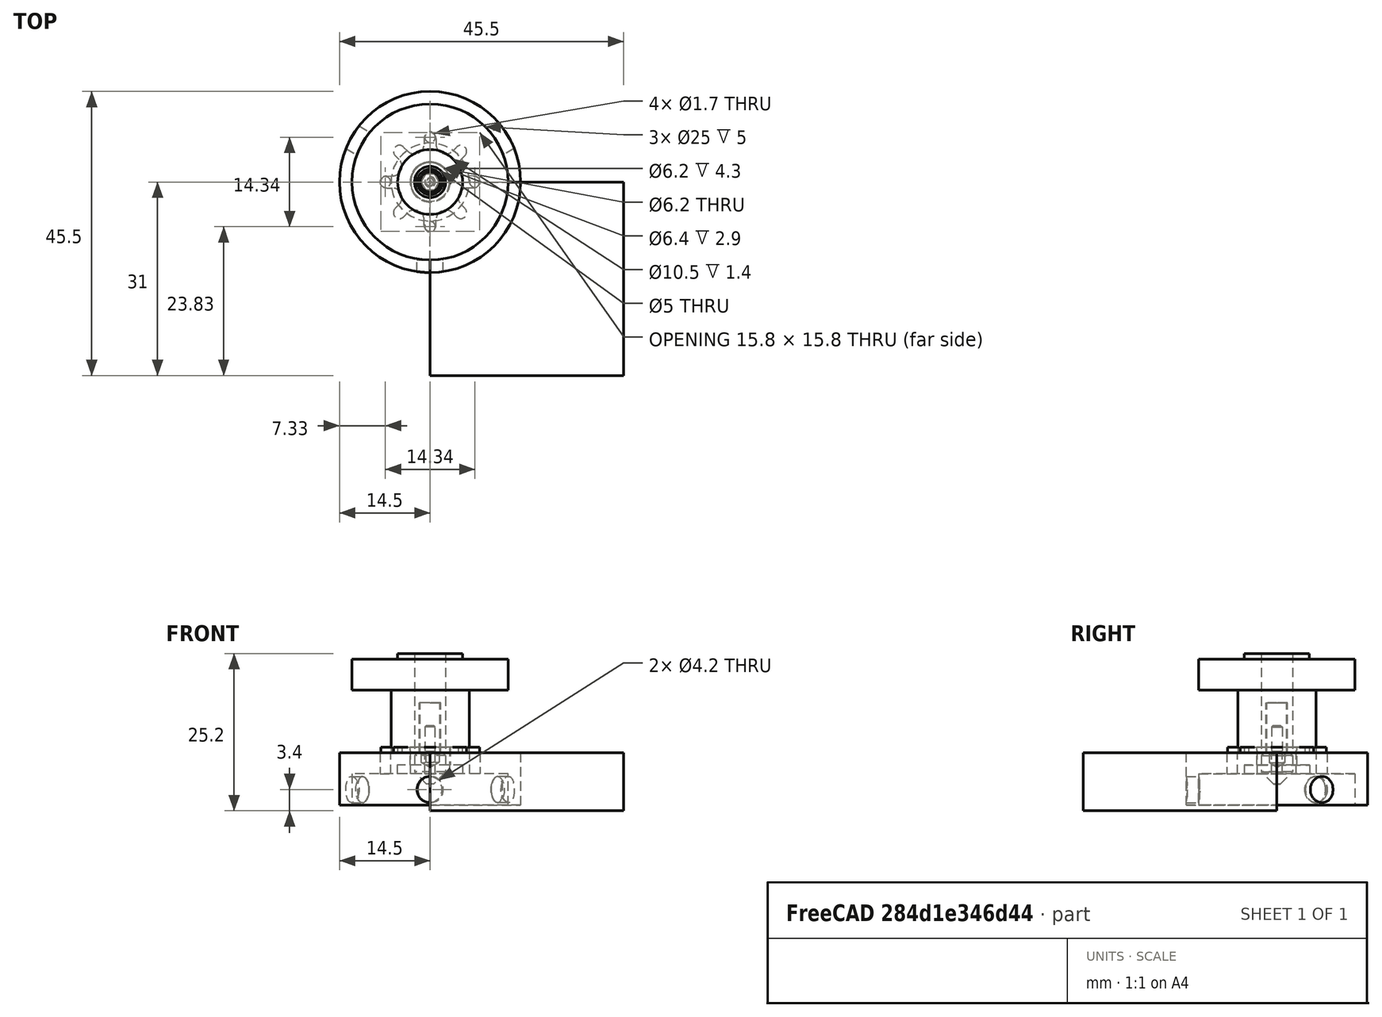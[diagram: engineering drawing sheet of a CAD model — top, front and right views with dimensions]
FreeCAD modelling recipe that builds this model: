
FCSTD DOCUMENT  (FreeCAD 0.22R35858 (Git))
Label: FeinMultiTool
License: All rights reserved
LicenseURL: http://en.wikipedia.org/wiki/All_rights_reserved
objects: Sketcher::SketchObject×21, TechDraw::DrawViewDimension×18, Path::FeaturePython×17, PartDesign::Pad×10, PartDesign::Pocket×8, App::Part×6, PartDesign::Body×5, Part::FeaturePython×5, PartDesign::PolarPattern×5, TechDraw::DrawViewPart×5, App::DocumentObjectGroup×5, PartDesign::Hole×3, PartDesign::CoordinateSystem×2, TechDraw::DrawSVGTemplate×2, TechDraw::DrawPage×2, Spreadsheet::Sheet×1, PartDesign::Chamfer×1, App::FeaturePython×1
note: 116 computed .brp shape members not serialized (recipe doc carries the construction recipe); baked Part::Feature solids carry a one-line shape summary decoded from their .brp

FEATURE [Spreadsheet::Sheet] Spreadsheet
  Configuration = 2
  cells = A4='Part; B4='BaseThickness; C4='BaseDiameter; D4='WallThickness; E4='WallThicknessTop; F4='ShoulderDiameterInner; G4='ShoulderHeight; H4='PocketDepth; I4='PinDiameter; J4='PinBoltCircle; K4='PinCount; L4='StudAngle; M4='ScrewSize; N4='ScrewThreadSize; O4='ScrewLength; P4='ScrewCount; Q4='BoltHoleDiameter; R4='Chamfer; A5==hiddenref(.Configuration.String); B5(BaseThickness)==.B8; C5(BaseDiameter)==.C8; D5(WallThickness)==.D8; E5(WallThicknessTop)==.E8; F5(ShoulderDiameter)==.F8; G5(ShoulderHeight)==.G8; H5(PocketDepth)==.H8; I5(PinDiameter)==.I8; J5(PinBoltCircle)==.J8; K5(PinCount)==.K8; L5(StudAngle)==.L8; M5(ScrewSize)==.M8; N5(ScrewThreadSize)==.N8; O5(ScrewLength)==.O8; P5(ScrewCount)==.P8; Q5(BoltHoleDiameter)==.Q8; R5(Chamfer)==.R8; A6='Fein MXSE636 PinStyle Starlink Fine; B6=5; C6=25; D6=5; E6=2; F6=10.3; G6=0.9; H6=5; I6=2.1; J6=22.5; K6=4; L6=20; M6='M5; N6=4.2; O6=5; P6=3; Q6=6; R6=0.5; A7='Fein MXSE636 Starlink bolton type; B7=5; C7=25; D7=5; E7=2; F7=10.3; G7=0.9; H7=6; I7=1.7; J7=14.34; K7=4; L7=20; M7='M5; N7=4.2; O7=5; P7=3; Q7=6; R7=0.5; A8='Fein MXSE636 Starlink Glue type; B8=5; C8=25; D8=2; E8=2; F8=10.4; G8=0.9; H8=5; I8=1.7; J8=14.34; K8=4; L8=20; M8='M5; N8=4.2; O8=5; P8=3; Q8=6.2; R8=0.02; A12='CalculatedFields; A14='PinLength; B14(PinLength)==BodyThickness - PocketDepth + ShoulderHeight; A15='ScrewPositionV; B15(ScrewPositionV)==BodyThickness - PocketDepth + BaseThickness / 2; A16='OuterDiameter; B16(OuterDiameter)==BaseDiameter + WallThickness * 2; A17='BodyThickness; B17(BodyThickness)==PocketDepth + ShoulderHeight + 0.5 + WallThicknessTop; A19='StarLinkData; C19='Last values; A20='StarLinkTopDiameter; B20(StarLinkTopDiameter)=1.9; C20=1.7; D20=1.8; E20=1.9; F20=1.9; G20=1.9; A21='StarLinkBottomDiameter; B21(StarLinkBottomDiameter)=3.1; C21=3.3; D21=3.3; E21=3.3; F21=3.2; G21=3.2; A22='StarLinkDiameterOuter; B22(StarLinkDiameterOuter)=15.8; C22=15.8; D22=15.8; E22=15.8; F22=15.8; G22=15.8; A23='StarLinkDiameterInner; B23(StarLinkDiameterInner)=10; C23=10.1; D23=10.1; E23=10.1; F23=10.1; G23=10; A25='StarlinkBodyDiameter; B25(StarlinkBodyDiameter)==BaseDiameter + WallThickness * 2; A28='EndMillDiameter; B28(EndMillDiameter)=3; A29='EndMillDiameterFinish; B29(EndMillDiameterFinish)=3; A30='ChipLoad; B30(ChipLoad)=0.03; A31='ChipLoadFinish; B31(ChipLoadFinish)=0.02; A32='RPM; B32(RPM)=3000; A33='Flutes; B33(Flutes)=2; A35='FeedRate; B35(FeedRate)==RPM * ChipLoad * Flutes * 1 mm / min; A36='FeedRateFinish; B36(FeedRateFinish)==RPM * ChipLoadFinish * Flutes * 1 mm / min; A37='CuttingDepth; B37(CuttingDepth)=1; D37='0.9 mm default; A38='StepDown; B38(StepDown)=0.45; A39='FinishStepDown; B39(FinishStepDown)=0.1; A40='FacingDepth; B40(FacingDepth)=0.1; A42='StepOver; B42(StepOver)==EndMillDiameter * 0.9; A43='StepOverFinal; B43(StepOverFinal)=0.25; C45='Diameter Inner; A46='ExtraOffsetRoughing; B46(ExtraOffsetRoughing)==EndMillDiameter * 0.9; C46==OuterDiameter - ExtraOffsetRoughing * 2; A47='StockToLeaveProfilePass; B47(StockToLeaveProfilePass)=0.2; A48='StockToLeaveFinishPass; B48(StockToLeaveFinishPass)==-0.05
  expr: .Configuration.Enum = cells[<<A6:|>>]
  expr: .cells.Bind.B5.ZZ5 = tuple(.cells; <<B>> + str(hiddenref(Configuration) + 6); <<ZZ>> + str(hiddenref(Configuration) + 6))
FEATURE [Sketcher::SketchObject] Sketch
  FullyConstrained = true
  MapMode = 5
  Support = -> [XY_Plane001]
  expr: Constraints[1] = Spreadsheet.OuterDiameter
  expr: Constraints[3] = Spreadsheet.BoltHoleDiameter
  sketch-geometry (2):
    g0: Circle CenterX=0 CenterY=0 CenterZ=0 NormalX=0 NormalY=0 NormalZ=1 AngleXU=0 Radius=14.5
    g1: Circle CenterX=0 CenterY=0 CenterZ=0 NormalX=0 NormalY=0 NormalZ=1 AngleXU=0 Radius=3.1
  constraints (4):
    c: Coincident(g0,g-1)
    c: Diameter(g0) = 29
    c: Coincident(g1,g0)
    c: Diameter(g1) = 6.2
FEATURE [PartDesign::Pad] Pad  label="Body"
  Direction = (0,0,1)
  Length = 8.4
  Length2 = 10
  Profile = -> Sketch
  ReferenceAxis = -> Sketch [N_Axis]
  Reversed = true
  Type = 0
  expr: Length = Spreadsheet.BodyThickness
FEATURE [Sketcher::SketchObject] Sketch001
  AttachmentOffset = pos=(0,0,-8.4) rot=(0,0,1;0rad)
  FullyConstrained = true
  MapMode = 5
  Placement = pos=(0,0,-8.4) rot=(0,0,1;0rad)
  Support = -> [XY_Plane001]
  expr: .AttachmentOffset.Base.z = -Spreadsheet.BodyThickness
  expr: Constraints[1] = Spreadsheet.BaseDiameter
  sketch-geometry (1):
    g0: Circle CenterX=0 CenterY=0 CenterZ=0 NormalX=0 NormalY=0 NormalZ=1 AngleXU=0 Radius=12.5
  constraints (2):
    c: Coincident(g0,g-1)
    c: Diameter(g0) = 25
FEATURE [Sketcher::SketchObject] Sketch002
  FullyConstrained = true
  MapMode = 5
  Support = -> [XY_Plane001]
  expr: Constraints[0] = Spreadsheet.PinDiameter
  expr: Constraints[3] = Spreadsheet.PinBoltCircle
  sketch-geometry (2):
    g0: Circle CenterX=7.17 CenterY=0 CenterZ=0 NormalX=0 NormalY=0 NormalZ=1 AngleXU=0 Radius=0.85
    g1: Circle CenterX=0 CenterY=0 CenterZ=0 NormalX=0 NormalY=0 NormalZ=1 AngleXU=0 Radius=7.17
  constraints (5):
    c: Diameter(g0) = 1.7
    c: Coincident(g1,g-1)
    c: PointOnObject(g0,g1)
    c: Diameter(g1) = 14.34
    c: PointOnObject(g0,g-1)
FEATURE [Sketcher::SketchObject] Sketch003
  AttachmentOffset = pos=(0,0,14.5) rot=(0,0,1;0rad)
  FullyConstrained = true
  MapMode = 5
  Placement = pos=(0,-14.5,3.2e-15) rot=(1,0,0;1.5708rad)
  Support = -> [XZ_Plane001]
  expr: .AttachmentOffset.Base.z = Spreadsheet.OuterDiameter / 2
  expr: Constraints[1] = Spreadsheet.ScrewThreadSize
  expr: Constraints[2] = Spreadsheet.ScrewPositionV
  sketch-geometry (1):
    g0: Circle CenterX=0 CenterY=-5.9 CenterZ=0 NormalX=0 NormalY=0 NormalZ=1 AngleXU=0 Radius=2.1
  constraints (3):
    c: PointOnObject(g0,g-2)
    c: Diameter(g0) = 4.2
    c: DistanceY(g0,g-1) = 5.9
FEATURE [Sketcher::SketchObject] Sketch004
  FullyConstrained = true
  MapMode = 5
  Support = -> [XY_Plane003]
  expr: Constraints[1] = Spreadsheet.PinDiameter
  sketch-geometry (1):
    g0: Circle CenterX=0 CenterY=0 CenterZ=0 NormalX=0 NormalY=0 NormalZ=1 AngleXU=0 Radius=0.85
  constraints (2):
    c: Coincident(g0,g-1)
    c: Diameter(g0) = 1.7
FEATURE [PartDesign::Pad] Pad001
  Direction = (0,0,1)
  Length = 4.3
  Length2 = 10
  Profile = -> Sketch004
  ReferenceAxis = -> Sketch004 [N_Axis]
  Type = 0
  expr: Length = Spreadsheet.PinLength
FEATURE [PartDesign::Chamfer] Chamfer
  Angle = 45
  Base = -> Pad001 [Face2,Face3]
  BaseFeature = -> Pad001
  ChamferType = 0
  FlipDirection = false
  Size = 0.2
  Size2 = 1
  SupportTransform = false
  UseAllEdges = false
FEATURE [PartDesign::Body] Body001  label="Body"
  Group = -> [Sketch004,Pad001,Chamfer]
  Origin = -> Origin003
  Tip = -> Chamfer
FEATURE [PartDesign::CoordinateSystem] flange
  AttacherType = Attacher::AttachEngine3D
  MapMode = 11
  Placement = pos=(0,0,0) rot=(0,0,1;1.5708rad)
  Support = -> [Chamfer]
FEATURE [App::Part] Part001  label="Stud"
  Group = -> [Body001,flange]
  Origin = -> Origin002
FEATURE [Part::FeaturePython] Screw  label="M5x5-Screw"  # Fasteners workbench fastener (typed FeaturePython)
  diameter = 8
  invert = false
  leftHanded = false
  length = 0
  lengthCustom = 5
  matchOuter = false
  offset = 0
  thread = false
  type = 45
FEATURE [PartDesign::CoordinateSystem] Flange
  AttacherType = Attacher::AttachEngine3D
  Support = -> [Screw]
FEATURE [App::Part] Part002  label="GrubScrew"
  Group = -> [Screw,Flange]
  Origin = -> Origin006
FEATURE [Sketcher::SketchObject] Sketch005
  FullyConstrained = true
  MapMode = 5
  Support = -> [XY_Plane001]
  expr: Constraints[1] = Spreadsheet.ShoulderDiameter
  sketch-geometry (1):
    g0: Circle CenterX=0 CenterY=0 CenterZ=0 NormalX=0 NormalY=0 NormalZ=1 AngleXU=0 Radius=5.2
  constraints (2):
    c: Coincident(g0,g-1)
    c: Diameter(g0) = 10.4
FEATURE [PartDesign::Pad] Pad002  label="Shoulder"
  BaseFeature = -> Pad
  Direction = (0,0,1)
  Length = 0.9
  Length2 = 10
  Profile = -> Sketch005
  ReferenceAxis = -> Sketch005 [N_Axis]
  Type = 0
  expr: Length = Spreadsheet.ShoulderHeight
FEATURE [Sketcher::SketchObject] Sketch006
  FullyConstrained = true
  MapMode = 5
  Support = -> [XY_Plane001]
  expr: Constraints[1] = Spreadsheet.OuterDiameter
  expr: Constraints[3] = Spreadsheet.BoltHoleDiameter
  sketch-geometry (2):
    g0: Circle CenterX=0 CenterY=0 CenterZ=0 NormalX=0 NormalY=0 NormalZ=1 AngleXU=0 Radius=14.5
    g1: Circle CenterX=0 CenterY=0 CenterZ=0 NormalX=0 NormalY=0 NormalZ=1 AngleXU=0 Radius=3.1
  constraints (4):
    c: Coincident(g0,g-1)
    c: Diameter(g0) = 29
    c: Coincident(g1,g0)
    c: Diameter(g1) = 6.2
FEATURE [PartDesign::Pocket] Pocket002  label="BoltPocket"
  BaseFeature = -> Pad002
  Direction = (0,0,-1)
  Length = 5
  Length2 = 5
  Midplane = true
  Profile = -> Sketch006
  ReferenceAxis = -> Sketch006 [N_Axis]
  Type = 1
FEATURE [PartDesign::Pocket] Pocket  label="BasePocket"
  BaseFeature = -> Pocket002
  Direction = (0,0,-1)
  Length = 5
  Length2 = 5
  Profile = -> Sketch001
  ReferenceAxis = -> Sketch001 [N_Axis]
  Reversed = true
  Type = 0
  expr: Length = Spreadsheet.PocketDepth
FEATURE [PartDesign::Hole] Hole  label="LockScrewHole"
  BaseFeature = -> Pocket
  CustomThreadClearance = 0
  Depth = 2
  DepthType = 0
  Diameter = 4.2
  DrillForDepth = false
  DrillPoint = 1
  DrillPointAngle = 118
  HoleCutCountersinkAngle = 90
  HoleCutCustomValues = false
  HoleCutDepth = 0
  HoleCutDiameter = 6.1
  HoleCutType = 0
  ModelThread = false
  Profile = -> Sketch003
  Tapered = false
  TaperedAngle = 90
  ThreadClass = 0
  ThreadDepth = 2
  ThreadDepthType = 0
  ThreadDirection = 0
  ThreadFit = 0
  ThreadSize = 13
  ThreadType = 1
  Threaded = true
  UseCustomThreadClearance = false
  expr: Depth = Spreadsheet.WallThickness
FEATURE [PartDesign::PolarPattern] PolarPattern001  label="LockScrewHoles"
  Angle = 360
  Axis = -> Z_Axis001
  BaseFeature = -> Hole
  Mode = 0
  Occurrences = 3
  Offset = 120
  Originals = -> [Hole]
  expr: Occurrences = Spreadsheet.ScrewCount
FEATURE [PartDesign::Pocket] Pocket001  label="PinPocket"
  BaseFeature = -> PolarPattern001
  Direction = (0,0,-1)
  Length = 5
  Length2 = 5
  Profile = -> Sketch002
  ReferenceAxis = -> Sketch002 [N_Axis]
  Type = 1
FEATURE [PartDesign::PolarPattern] PolarPattern  label="PinPockets"
  Angle = 360
  Axis = -> Sketch002 [N_Axis]
  BaseFeature = -> Pocket001
  Mode = 0
  Occurrences = 4
  Offset = 120
  Originals = -> [Pocket001]
  expr: Occurrences = Spreadsheet.PinCount
FEATURE [PartDesign::Body] Body
  Group = -> [Pad,Pad002,Pocket002,Sketch,Sketch005,Sketch001,Pocket,Hole,PolarPattern001,Sketch002,Pocket001,PolarPattern,Sketch003,Sketch006]
  Origin = -> Origin001
  Tip = -> PolarPattern
FEATURE [App::Part] Part  label="PinApter"
  Group = -> [Body]
  Origin = -> Origin
FEATURE [Sketcher::SketchObject] Sketch007
  FullyConstrained = true
  MapMode = 5
  Support = -> [XY_Plane007]
  expr: Constraints[1] = Spreadsheet.OuterDiameter
  expr: Constraints[3] = Spreadsheet.BoltHoleDiameter
  sketch-geometry (2):
    g0: Circle CenterX=0 CenterY=0 CenterZ=0 NormalX=0 NormalY=0 NormalZ=1 AngleXU=0 Radius=14.5
    g1: Circle CenterX=0 CenterY=0 CenterZ=0 NormalX=0 NormalY=0 NormalZ=1 AngleXU=0 Radius=3.1
  constraints (4):
    c: Coincident(g0,g-1)
    c: Diameter(g0) = 29
    c: Coincident(g1,g0)
    c: Diameter(g1) = 6.2
FEATURE [PartDesign::Pad] Pad003  label="Body"
  Direction = (0,0,1)
  Length = 8.4
  Length2 = 10
  Profile = -> Sketch007
  ReferenceAxis = -> Sketch007 [N_Axis]
  Reversed = true
  Type = 0
  expr: Length = Spreadsheet.BodyThickness
FEATURE [Sketcher::SketchObject] Sketch008
  AttachmentOffset = pos=(0,0,-8.4) rot=(0,0,1;0rad)
  FullyConstrained = true
  MapMode = 5
  Placement = pos=(0,0,-8.4) rot=(0,0,1;0rad)
  Support = -> [XY_Plane007]
  expr: .AttachmentOffset.Base.z = -Spreadsheet.BodyThickness
  expr: Constraints[1] = Spreadsheet.BaseDiameter
  sketch-geometry (1):
    g0: Circle CenterX=0 CenterY=0 CenterZ=0 NormalX=0 NormalY=0 NormalZ=1 AngleXU=0 Radius=12.5
  constraints (2):
    c: Coincident(g0,g-1)
    c: Diameter(g0) = 25
FEATURE [Sketcher::SketchObject] Sketch010
  AttachmentOffset = pos=(0,0,14.5) rot=(0,0,1;0rad)
  FullyConstrained = true
  MapMode = 5
  Placement = pos=(0,-14.5,3.2e-15) rot=(1,0,0;1.5708rad)
  Support = -> [XZ_Plane007]
  expr: .AttachmentOffset.Base.z = Spreadsheet.OuterDiameter / 2
  expr: Constraints[1] = Spreadsheet.ScrewThreadSize
  expr: Constraints[2] = Spreadsheet.ScrewPositionV
  sketch-geometry (1):
    g0: Circle CenterX=0 CenterY=-5.9 CenterZ=0 NormalX=0 NormalY=0 NormalZ=1 AngleXU=0 Radius=2.1
  constraints (3):
    c: PointOnObject(g0,g-2)
    c: Diameter(g0) = 4.2
    c: DistanceY(g0,g-1) = 5.9
FEATURE [Sketcher::SketchObject] Sketch011
  FullyConstrained = true
  MapMode = 5
  Support = -> [XY_Plane007]
  expr: Constraints[1] = Spreadsheet.StarLinkDiameterInner
  expr: Constraints[2] = Spreadsheet.StarLinkTopDiameter
  expr: Constraints[5] = Spreadsheet.StarLinkDiameterOuter
  expr: Constraints[7] = Spreadsheet.StarLinkBottomDiameter
  sketch-geometry (11):
    g0: ArcOfCircle CenterX=0 CenterY=0 CenterZ=0 NormalX=0 NormalY=0 NormalZ=1 AngleXU=0 Radius=5 StartAngle=1.1781 EndAngle=1.9635
    g1: ArcOfCircle CenterX=0 CenterY=6.95 CenterZ=0 NormalX=0 NormalY=0 NormalZ=1 AngleXU=0 Radius=0.95 StartAngle=0.00724552 EndAngle=3.13435
    g2: Circle CenterX=0 CenterY=0 CenterZ=0 NormalX=0 NormalY=0 NormalZ=1 AngleXU=0 Radius=7.9
    g3: ArcOfCircle CenterX=-2.50658 CenterY=6.05141 CenterZ=0 NormalX=0 NormalY=0 NormalZ=1 AngleXU=0 Radius=1.55 StartAngle=5.10509 EndAngle=6.27594
    g4: ArcOfCircle CenterX=2.50658 CenterY=6.05141 CenterZ=0 NormalX=0 NormalY=0 NormalZ=1 AngleXU=0 Radius=1.55 StartAngle=3.14884 EndAngle=4.31969
    g5: LineSegment StartX=-0.949975 StartY=6.95688 StartZ=0 EndX=-0.956617 EndY=6.04018 EndZ=0
    g6: LineSegment StartX=0.949975 StartY=6.95688 StartZ=0 EndX=0.956617 EndY=6.04018 EndZ=0
    g7: LineSegment StartX=-2.50658 StartY=6.05141 StartZ=0 EndX=0 EndY=0 EndZ=0
    g8: LineSegment StartX=0 StartY=0 StartZ=0 EndX=2.50658 EndY=6.05141 EndZ=0
    g9: LineSegment StartX=-1.91342 StartY=4.6194 StartZ=0 EndX=-2e-16 EndY=0 EndZ=0
    g10: LineSegment StartX=0 StartY=0 StartZ=0 EndX=1.91342 EndY=4.6194 EndZ=0
  constraints (25):
    c: PointOnObject(g1,g-2)
    c: Diameter(g0) = 10
    c: Diameter(g1) = 1.9
    c: Coincident(g2,g-1)
    c: Coincident(g0,g2)
    c: Diameter(g2) = 15.8
    c: Tangent(g1,g2)
    c: Diameter(g3) = 3.1
    c: Equal(g3,g4)
    c: Coincident(g7,g3)
    c: Coincident(g7,g0)
    c: Coincident(g8,g0)
    c: Coincident(g8,g4)
    c: Angle(g8,g7) = 0.785398
    c: Horizontal(g3,g4)
    c: Tangent(g1,g5) = -1.5708
    c: Tangent(g1,g6) = 1.5708
    c: Tangent(g3,g5) = 1.5708
    c: Tangent(g4,g6) = -1.5708
    c: Tangent(g0,g3) = 1.5708
    c: Tangent(g0,g4) = 1.5708
    c: Coincident(g9,g3)
    c: Coincident(g9,g0)
    c: Coincident(g10,g9)
    c: Coincident(g10,g4)
FEATURE [PartDesign::Pad] Pad004  label="StarLinkShoulder"
  BaseFeature = -> Pad003
  Direction = (0,0,1)
  Length = 0.9
  Length2 = 10
  Profile = -> Sketch011
  ReferenceAxis = -> Sketch011 [N_Axis]
  Type = 0
  expr: Length = Spreadsheet.ShoulderHeight
FEATURE [PartDesign::PolarPattern] PolarPattern004  label="StarLink"
  Angle = 360
  Axis = -> Sketch011 [N_Axis]
  BaseFeature = -> Pad004
  Mode = 0
  Occurrences = 8
  Offset = 120
  Originals = -> [Pad004]
FEATURE [Sketcher::SketchObject] Sketch012
  FullyConstrained = true
  MapMode = 5
  Support = -> [XY_Plane007]
  expr: Constraints[1] = Spreadsheet.OuterDiameter
  expr: Constraints[3] = Spreadsheet.BoltHoleDiameter
  sketch-geometry (2):
    g0: Circle CenterX=0 CenterY=0 CenterZ=0 NormalX=0 NormalY=0 NormalZ=1 AngleXU=0 Radius=14.5
    g1: Circle CenterX=0 CenterY=0 CenterZ=0 NormalX=0 NormalY=0 NormalZ=1 AngleXU=0 Radius=3.1
  constraints (4):
    c: Coincident(g0,g-1)
    c: Diameter(g0) = 29
    c: Coincident(g1,g0)
    c: Diameter(g1) = 6.2
FEATURE [PartDesign::Pocket] Pocket005  label="BoltPocket"
  BaseFeature = -> PolarPattern004
  Direction = (0,0,-1)
  Length = 5
  Length2 = 5
  Midplane = true
  Profile = -> Sketch012
  ReferenceAxis = -> Sketch012 [N_Axis]
  Type = 1
FEATURE [PartDesign::Pocket] Pocket003  label="BodyPocket"
  BaseFeature = -> Pocket005
  Direction = (0,0,-1)
  Length = 5
  Length2 = 5
  Profile = -> Sketch008
  ReferenceAxis = -> Sketch008 [N_Axis]
  Reversed = true
  Type = 0
  expr: Length = Spreadsheet.PocketDepth
FEATURE [PartDesign::Hole] Hole005  label="SrewHole"
  BaseFeature = -> Pocket003
  CustomThreadClearance = 0
  Depth = 2
  DepthType = 0
  Diameter = 4.2
  DrillForDepth = false
  DrillPoint = 1
  DrillPointAngle = 118
  HoleCutCountersinkAngle = 90
  HoleCutCustomValues = false
  HoleCutDepth = 0
  HoleCutDiameter = 6.1
  HoleCutType = 0
  ModelThread = false
  Profile = -> Sketch010
  Tapered = false
  TaperedAngle = 90
  ThreadClass = 0
  ThreadDepth = 2
  ThreadDepthType = 0
  ThreadDirection = 0
  ThreadFit = 0
  ThreadSize = 13
  ThreadType = 1
  Threaded = true
  UseCustomThreadClearance = false
  expr: Depth = Spreadsheet.WallThickness
FEATURE [PartDesign::PolarPattern] PolarPattern003  label="ScrewHoles"
  Angle = 360
  Axis = -> Z_Axis007
  BaseFeature = -> Hole005
  Mode = 0
  Occurrences = 3
  Offset = 120
  Originals = -> [Hole005]
  expr: Occurrences = Spreadsheet.ScrewCount
FEATURE [PartDesign::Body] Body002
  Group = -> [Pad003,Pad004,PolarPattern004,Pocket005,Sketch007,Sketch011,Sketch008,Pocket003,Sketch010,Hole005,PolarPattern003,Sketch012]
  Origin = -> Origin008
  Tip = -> PolarPattern003
FEATURE [App::Part] Part003  label="StarlockAdapter Bolt On Type"
  Group = -> [Body002]
  Origin = -> Origin007
FEATURE [Sketcher::SketchObject] Sketch013
  FullyConstrained = true
  MapMode = 5
  Support = -> [XY_Plane009]
  expr: Constraints[1] = Spreadsheet.StarlinkBodyDiameter
  expr: Constraints[3] = Spreadsheet.BoltHoleDiameter
  sketch-geometry (2):
    g0: Circle CenterX=0 CenterY=0 CenterZ=0 NormalX=0 NormalY=0 NormalZ=1 AngleXU=0 Radius=14.5
    g1: Circle CenterX=0 CenterY=0 CenterZ=0 NormalX=0 NormalY=0 NormalZ=1 AngleXU=0 Radius=3.1
  constraints (4):
    c: Coincident(g0,g-1)
    c: Diameter(g0) = 29
    c: Coincident(g1,g0)
    c: Diameter(g1) = 6.2
FEATURE [PartDesign::Pad] Pad005  label="Body"
  Direction = (0,0,1)
  Length = 8.4
  Length2 = 10
  Profile = -> Sketch013
  ReferenceAxis = -> Sketch013 [N_Axis]
  Reversed = true
  Type = 0
  expr: Length = Spreadsheet.BodyThickness
FEATURE [Sketcher::SketchObject] Sketch016
  FullyConstrained = true
  MapMode = 5
  Support = -> [XY_Plane009]
  expr: Constraints[1] = Spreadsheet.StarLinkDiameterInner
  expr: Constraints[2] = Spreadsheet.StarLinkTopDiameter
  expr: Constraints[5] = Spreadsheet.StarLinkDiameterOuter
  expr: Constraints[7] = Spreadsheet.StarLinkBottomDiameter
  sketch-geometry (11):
    g0: ArcOfCircle CenterX=0 CenterY=0 CenterZ=0 NormalX=0 NormalY=0 NormalZ=1 AngleXU=0 Radius=5 StartAngle=1.1781 EndAngle=1.9635
    g1: ArcOfCircle CenterX=0 CenterY=6.95 CenterZ=0 NormalX=0 NormalY=0 NormalZ=1 AngleXU=0 Radius=0.95 StartAngle=0.00724552 EndAngle=3.13435
    g2: Circle CenterX=0 CenterY=0 CenterZ=0 NormalX=0 NormalY=0 NormalZ=1 AngleXU=0 Radius=7.9
    g3: ArcOfCircle CenterX=-2.50658 CenterY=6.05141 CenterZ=0 NormalX=0 NormalY=0 NormalZ=1 AngleXU=0 Radius=1.55 StartAngle=5.10509 EndAngle=6.27594
    g4: ArcOfCircle CenterX=2.50658 CenterY=6.05141 CenterZ=0 NormalX=0 NormalY=0 NormalZ=1 AngleXU=0 Radius=1.55 StartAngle=3.14884 EndAngle=4.31969
    g5: LineSegment StartX=-0.949975 StartY=6.95688 StartZ=0 EndX=-0.956617 EndY=6.04018 EndZ=0
    g6: LineSegment StartX=0.949975 StartY=6.95688 StartZ=0 EndX=0.956617 EndY=6.04018 EndZ=0
    g7: LineSegment StartX=-2.50658 StartY=6.05141 StartZ=0 EndX=0 EndY=0 EndZ=0
    g8: LineSegment StartX=0 StartY=0 StartZ=0 EndX=2.50658 EndY=6.05141 EndZ=0
    g9: LineSegment StartX=-1.91342 StartY=4.6194 StartZ=0 EndX=0 EndY=0 EndZ=0
    g10: LineSegment StartX=0 StartY=0 StartZ=0 EndX=1.91342 EndY=4.6194 EndZ=0
  constraints (25):
    c: PointOnObject(g1,g-2)
    c: Diameter(g0) = 10
    c: Diameter(g1) = 1.9
    c: Coincident(g2,g-1)
    c: Coincident(g0,g2)
    c: Diameter(g2) = 15.8
    c: Tangent(g1,g2)
    c: Diameter(g3) = 3.1
    c: Equal(g3,g4)
    c: Coincident(g7,g3)
    c: Coincident(g7,g0)
    c: Coincident(g8,g0)
    c: Coincident(g8,g4)
    c: Angle(g8,g7) = 0.785398
    c: Horizontal(g3,g4)
    c: Tangent(g1,g5) = -1.5708
    c: Tangent(g1,g6) = 1.5708
    c: Tangent(g3,g5) = 1.5708
    c: Tangent(g4,g6) = -1.5708
    c: Tangent(g0,g3) = 1.5708
    c: Tangent(g0,g4) = 1.5708
    c: Coincident(g9,g3)
    c: Coincident(g9,g0)
    c: Coincident(g10,g9)
    c: Coincident(g10,g4)
FEATURE [PartDesign::Pad] Pad006  label="StarLockShoulder"
  BaseFeature = -> Pad005
  Direction = (0,0,1)
  Length = 0.9
  Length2 = 10
  Profile = -> Sketch016
  ReferenceAxis = -> Sketch016 [N_Axis]
  Type = 0
  expr: Length = 0.9
FEATURE [PartDesign::PolarPattern] PolarPattern006
  Angle = 360
  Axis = -> Sketch016 [N_Axis]
  BaseFeature = -> Pad006
  Mode = 0
  Occurrences = 8
  Offset = 120
  Originals = -> [Pad006]
FEATURE [App::FeaturePython] SetupSheet  # Path/CAM operation (typed FeaturePython)
  ClearanceHeightExpression = OpStockZMax+SetupSheet.ClearanceHeightOffset
  ClearanceHeightOffset = 5
  CoolantMode = 1
  CoolantModes = None | Flood | Mist
  FinalDepthExpression = OpFinalDepth
  HorizRapid = 0
  SafeHeightExpression = OpStockZMax+SetupSheet.SafeHeightOffset
  SafeHeightOffset = 0.5
  StartDepthExpression = OpStartDepth
  StepDownExpression = OpToolDiameter
  VertRapid = 0
FEATURE [Part::FeaturePython] ToolBit001  label="EndMill"  # Path/CAM toolbit (typed FeaturePython)
  BitPropertyNames = Chipload | CuttingEdgeHeight | Diameter | Flutes | Length | Material | ShankDiameter | SpindleDirection
  BitShape = <path>
  Chipload = 0.14
  CuttingEdgeHeight = 8
  Diameter = 3
  File = <path>
  Flutes = 2
  Length = 0
  Material = 0
  ShankDiameter = 0
  ShapeName = endmill
  SpindleDirection = 0
  expr: Diameter = Spreadsheet.EndMillDiameter
FEATURE [Path::FeaturePython] __mmEndMill  label="EndMill Rouhing"  # Path/CAM operation (typed FeaturePython)
  HorizFeed = 3
  HorizRapid = 0
  SpindleDir = 0
  SpindleSpeed = 3000
  Tool = -> ToolBit001
  ToolNumber = 2
  VertFeed = 0.333333
  VertRapid = 0
  expr: HorizFeed = Spreadsheet.FeedRate
  expr: HorizRapid = SetupSheet.HorizRapid
  expr: SpindleSpeed = Spreadsheet.RPM
  expr: VertRapid = SetupSheet.VertRapid
FEATURE [Sketcher::SketchObject] Sketch017
  AttachmentOffset = pos=(0,0,-3.4) rot=(0,0,1;0rad)
  FullyConstrained = true
  MapMode = 5
  Placement = pos=(0,0,-3.4) rot=(0,0,1;0rad)
  Support = -> [XY_Plane009]
  expr: .AttachmentOffset.Base.z = -Spreadsheet.BodyThickness + Spreadsheet.PocketDepth
  sketch-geometry (1):
    g0: Circle CenterX=0 CenterY=0 CenterZ=0 NormalX=0 NormalY=0 NormalZ=1 AngleXU=0 Radius=5.25
  constraints (2):
    c: Coincident(g0,g-1)
    c: Diameter(g0) = 10.5
FEATURE [Sketcher::SketchObject] Sketch018
  FullyConstrained = true
  MapMode = 5
  Support = -> [XY_Plane009]
  expr: Constraints[1] = 6.4
  sketch-geometry (1):
    g0: Circle CenterX=0 CenterY=0 CenterZ=0 NormalX=0 NormalY=0 NormalZ=1 AngleXU=0 Radius=3.2
  constraints (2):
    c: Coincident(g0,g-1)
    c: Diameter(g0) = 6.4
FEATURE [TechDraw::DrawSVGTemplate] Template
  EditableTexts = Designed_by_Name=Designed by Name; Drawing_number=Drawing number; FC-Date=Date; FC-SC=Scale; FC-SH=Sheet; FC-Title=Fein multimaster MSx636; Subtitle=Starlock adapter glue on type; Weight=Weight
  Height = 210
  Orientation = 1
  Template = C:/Program Files/FreeCADW20240123/data/Mod/TechDraw/Templates/A4_LandscapeTD.svg
  Width = 297
FEATURE [Sketcher::SketchObject] Sketch019
  FullyConstrained = true
  MapMode = 5
  Support = -> [XY_Plane011]
  sketch-geometry (1):
    g0: Circle CenterX=0 CenterY=0 CenterZ=0 NormalX=0 NormalY=0 NormalZ=1 AngleXU=0 Radius=6.25
  constraints (2):
    c: Coincident(g0,g-1)
    c: Diameter(g0) = 12.5
FEATURE [PartDesign::Pad] Pad007  label="Base"
  Direction = (0,0,1)
  Length = 10
  Length2 = 10
  Profile = -> Sketch019
  ReferenceAxis = -> Sketch019 [N_Axis]
  Type = 0
FEATURE [Sketcher::SketchObject] Sketch020
  FullyConstrained = true
  MapMode = 5
  Placement = pos=(0,0,10) rot=(0,0,1;0rad)
  Support = -> [Pad007]
  expr: Constraints[1] = Spreadsheet.BaseDiameter
  sketch-geometry (1):
    g0: Circle CenterX=0 CenterY=0 CenterZ=0 NormalX=0 NormalY=0 NormalZ=1 AngleXU=0 Radius=12.5
  constraints (2):
    c: Coincident(g0,g-1)
    c: Diameter(g0) = 25
FEATURE [PartDesign::Pad] Pad008  label="Holder"
  BaseFeature = -> Pad007
  Direction = (0,0,1)
  Length = 5
  Length2 = 10
  Profile = -> Sketch020
  ReferenceAxis = -> Sketch020 [N_Axis]
  Type = 0
  expr: Length = Spreadsheet.BaseThickness
FEATURE [Sketcher::SketchObject] Sketch021
  FullyConstrained = true
  MapMode = 5
  Placement = pos=(0,0,15) rot=(0,0,1;0rad)
  Support = -> [Pad008]
  expr: Constraints[1] = Spreadsheet.ShoulderDiameter
  sketch-geometry (1):
    g0: Circle CenterX=0 CenterY=0 CenterZ=0 NormalX=0 NormalY=0 NormalZ=1 AngleXU=0 Radius=5.2
  constraints (2):
    c: Coincident(g0,g-1)
    c: Diameter(g0) = 10.4
FEATURE [PartDesign::Pad] Pad009  label="Shoulder"
  BaseFeature = -> Pad008
  Direction = (0,0,1)
  Length = 0.9
  Length2 = 10
  Profile = -> Sketch021
  ReferenceAxis = -> Sketch021 [N_Axis]
  Type = 0
  expr: Length = Spreadsheet.ShoulderHeight
FEATURE [Sketcher::SketchObject] Sketch022
  FullyConstrained = false
  MapMode = 5
  Placement = pos=(0,0,15.9) rot=(0,0,1;0rad)
  Support = -> [Pad009]
  sketch-geometry (1):
    g0: Circle CenterX=0 CenterY=0 CenterZ=0 NormalX=0 NormalY=0 NormalZ=1 AngleXU=0 Radius=1.12325
  constraints (1):
    c: Coincident(g0,g-1)
FEATURE [PartDesign::Hole] Hole006  label="Thread"
  BaseFeature = -> Pad009
  CustomThreadClearance = 0
  Depth = 25
  DepthType = 0
  Diameter = 5
  DrillForDepth = false
  DrillPoint = 1
  DrillPointAngle = 118
  HoleCutCountersinkAngle = 90
  HoleCutCustomValues = false
  HoleCutDepth = 0
  HoleCutDiameter = 6.1
  HoleCutType = 0
  ModelThread = false
  Profile = -> Sketch022
  Tapered = false
  TaperedAngle = 90
  ThreadClass = 0
  ThreadDepth = 25
  ThreadDepthType = 0
  ThreadDirection = 0
  ThreadFit = 0
  ThreadSize = 14
  ThreadType = 1
  Threaded = true
  UseCustomThreadClearance = false
FEATURE [PartDesign::Body] Body004  label="Body"
  Group = -> [Sketch019,Pad007,Sketch020,Pad008,Sketch021,Pad009,Sketch022,Hole006]
  Origin = -> Origin012
  Tip = -> Hole006
FEATURE [App::Part] Part005  label="FeinTool"
  Group = -> [Body004]
  Origin = -> Origin011
FEATURE [TechDraw::DrawSVGTemplate] Template001
  EditableTexts = Designed_by_Name=Designed by Name; Drawing_number=Drawing number; FC-Date=Date; FC-SC=Scale; FC-SH=Sheet; FC-Title=Fein Multimaster MXSE636; Subtitle=Subtitle; Weight=Weight
  Height = 210
  Orientation = 1
  Template = C:/Program Files/FreeCADW20240130/data/Mod/TechDraw/Templates/A4_LandscapeTD.svg
  Width = 297
FEATURE [TechDraw::DrawViewPart] View002
  CoarseView = false
  Direction = (0.352632,-0.909738,0.219153)
  Focus = 100
  HardHidden = false
  IsoCount = 0
  IsoHidden = false
  IsoVisible = false
  LockPosition = false
  Perspective = false
  Rotation = 0
  Scale = 2
  ScaleType = 0
  ScrubCount = 0
  SeamHidden = false
  SeamVisible = false
  SmoothHidden = false
  SmoothVisible = true
  Source = -> [Part005]
  X = 249.893
  XDirection = (0.572832,0.395051,0.718191)
  Y = 161.652
FEATURE [TechDraw::DrawViewPart] View003
  CoarseView = false
  Direction = (0,-1,0)
  Focus = 100
  HardHidden = true
  IsoCount = 0
  IsoHidden = false
  IsoVisible = false
  LockPosition = false
  Perspective = false
  Rotation = 0
  Scale = 2
  ScaleType = 0
  ScrubCount = 0
  SeamHidden = false
  SeamVisible = false
  SmoothHidden = false
  SmoothVisible = true
  Source = -> [Part005]
  X = 148.791
  XDirection = (1,0,0)
  Y = 136.667
FEATURE [TechDraw::DrawViewPart] View004
  CoarseView = false
  Direction = (0,0,1)
  Focus = 100
  HardHidden = false
  IsoCount = 0
  IsoHidden = false
  IsoVisible = false
  LockPosition = false
  Perspective = false
  Rotation = 0
  Scale = 2
  ScaleType = 0
  ScrubCount = 0
  SeamHidden = false
  SeamVisible = false
  SmoothHidden = false
  SmoothVisible = true
  Source = -> [Part005]
  X = 56.679
  XDirection = (1,0,0)
  Y = 122.154
FEATURE [TechDraw::DrawViewDimension] Dimension011
  AngleOverride = false
  Arbitrary = false
  ArbitraryTolerances = false
  EqualTolerance = true
  ExtensionAngle = 0
  FormatSpec = %.2w
  FormatSpecOverTolerance = %+.2w
  FormatSpecUnderTolerance = %+.2w
  Inverted = false
  LineAngle = 0
  LockPosition = false
  MeasureType = 1
  OverTolerance = 0
  References2D = -> [View003]
  Rotation = 0
  Scale = 2
  ScaleType = 0
  TheoreticalExact = false
  Type = 1
  UnderTolerance = 0
  X = -0.422294
  Y = 27.1626
FEATURE [TechDraw::DrawViewDimension] Dimension012
  AngleOverride = false
  Arbitrary = false
  ArbitraryTolerances = false
  EqualTolerance = true
  ExtensionAngle = 0
  FormatSpec = %.2w
  FormatSpecOverTolerance = %+.2w
  FormatSpecUnderTolerance = %+.2w
  Inverted = false
  LineAngle = 0
  LockPosition = false
  MeasureType = 1
  OverTolerance = 0
  References2D = -> [View003]
  Rotation = 0
  Scale = 2
  ScaleType = 0
  TheoreticalExact = false
  Type = 1
  UnderTolerance = 0
  X = -0.527867
  Y = 35.2865
FEATURE [TechDraw::DrawViewDimension] Dimension013
  AngleOverride = false
  Arbitrary = false
  ArbitraryTolerances = false
  EqualTolerance = true
  ExtensionAngle = 0
  FormatSpec = %.2w
  FormatSpecOverTolerance = %+.2w
  FormatSpecUnderTolerance = %+.2w
  Inverted = false
  LineAngle = 0
  LockPosition = false
  MeasureType = 1
  OverTolerance = 0
  References2D = -> [View003]
  Rotation = 0
  Scale = 2
  ScaleType = 0
  TheoreticalExact = false
  Type = 2
  UnderTolerance = 0
  X = 37.3521
  Y = 11.3889
FEATURE [TechDraw::DrawViewDimension] Dimension015
  AngleOverride = false
  Arbitrary = false
  ArbitraryTolerances = false
  EqualTolerance = true
  ExtensionAngle = 0
  FormatSpec = %.2w
  FormatSpecOverTolerance = %+.2w
  FormatSpecUnderTolerance = %+.2w
  Inverted = false
  LineAngle = 0
  LockPosition = false
  MeasureType = 1
  OverTolerance = 0
  References2D = -> [View003]
  Rotation = 0
  Scale = 2
  ScaleType = 0
  TheoreticalExact = false
  Type = 2
  UnderTolerance = 0
  X = 15.3866
  Y = 25.4136
FEATURE [TechDraw::DrawViewDimension] Dimension016
  AngleOverride = false
  Arbitrary = true
  ArbitraryTolerances = false
  EqualTolerance = true
  ExtensionAngle = 0
  FormatSpec = M6
  FormatSpecOverTolerance = %+.2w
  FormatSpecUnderTolerance = %+.2w
  Inverted = false
  LineAngle = 0
  LockPosition = false
  MeasureType = 1
  OverTolerance = 0
  References2D = -> [View003]
  Rotation = 0
  Scale = 2
  ScaleType = 0
  TheoreticalExact = false
  Type = 1
  UnderTolerance = 0
  X = -16.2213
  Y = -19.7918
FEATURE [TechDraw::DrawPage] Page001  label="FeinTool"
  KeepUpdated = true
  NextBalloonIndex = 1
  ProjectionType = 0
  Scale = 2
  Template = -> Template001
  Views = -> [View002,View003,View004,Dimension011,Dimension012,Dimension013,Dimension015,Dimension016]
FEATURE [Part::FeaturePython] ToolBit002  label="EndMill"  # Path/CAM toolbit (typed FeaturePython)
  BitPropertyNames = Chipload | CuttingEdgeHeight | Diameter | Flutes | Length | Material | ShankDiameter | SpindleDirection
  BitShape = <path>
  Chipload = 0.05
  CuttingEdgeHeight = 8
  Diameter = 3
  File = <path>
  Flutes = 2
  Length = 0
  Material = 0
  ShankDiameter = 0
  ShapeName = endmill
  SpindleDirection = 0
  expr: Chipload = 0.05 mm
  expr: Diameter = Spreadsheet.EndMillDiameterFinish
FEATURE [Path::FeaturePython] __mmEndMill001  label="EndMill Finish"  # Path/CAM operation (typed FeaturePython)
  HorizFeed = 2
  HorizRapid = 0
  SpindleDir = 0
  SpindleSpeed = 3000
  Tool = -> ToolBit002
  ToolNumber = 2
  VertFeed = 0.333333
  VertRapid = 0
  expr: HorizFeed = Spreadsheet.FeedRateFinish
  expr: HorizRapid = SetupSheet.HorizRapid
  expr: SpindleSpeed = Spreadsheet.RPM
  expr: VertRapid = SetupSheet.VertRapid
FEATURE [App::DocumentObjectGroup] Tools
  Group = -> [__mmEndMill,__mmEndMill001]
FEATURE [Sketcher::SketchObject] Sketch023
  AttachmentOffset = pos=(0,0,-8.4) rot=(0,0,1;0rad)
  FullyConstrained = true
  MapMode = 5
  Placement = pos=(0,0,-8.4) rot=(0,0,1;0rad)
  Support = -> [XY_Plane009]
  expr: .AttachmentOffset.Base.z = -Spreadsheet.BodyThickness
  expr: Constraints[1] = Spreadsheet.BaseDiameter
  sketch-geometry (1):
    g0: Circle CenterX=0 CenterY=0 CenterZ=0 NormalX=0 NormalY=0 NormalZ=1 AngleXU=0 Radius=12.5
  constraints (2):
    c: Coincident(g0,g-1)
    c: Diameter(g0) = 25
FEATURE [PartDesign::Pocket] Pocket008  label="BasePocket"
  BaseFeature = -> PolarPattern006
  Direction = (0,0,-1)
  Length = 5
  Length2 = 5
  Profile = -> Sketch023
  ReferenceAxis = -> Sketch023 [N_Axis]
  Reversed = true
  Type = 0
  expr: Length = Spreadsheet.PocketDepth
FEATURE [PartDesign::Pocket] Pocket006  label="ShoulderBotomPocket"
  BaseFeature = -> Pocket008
  Direction = (0,0,-1)
  Length = 1.4
  Length2 = 5
  Profile = -> Sketch017
  ReferenceAxis = -> Sketch017 [N_Axis]
  Reversed = true
  Type = 0
  expr: Length = Spreadsheet.ShoulderHeight + 0.5
FEATURE [PartDesign::Pocket] Pocket007  label="BoltPocket"
  BaseFeature = -> Pocket006
  Direction = (0,0,-1)
  Length = 5
  Length2 = 5
  Midplane = true
  Profile = -> Sketch018
  ReferenceAxis = -> Sketch018 [N_Axis]
  Type = 1
FEATURE [PartDesign::Body] Body003  label="BodyStarlingGlueType"
  Group = -> [Pad005,Pad006,PolarPattern006,Pocket008,Sketch023,Sketch013,Sketch016,Sketch017,Pocket006,Sketch018,Pocket007]
  Origin = -> Origin010
  Tip = -> Pocket007
FEATURE [App::Part] Part004  label="Starlock Adapter Glue type"
  Group = -> [Body003]
  Origin = -> Origin009
FEATURE [Part::FeaturePython] Clone  label="Model-StarlinkAdapter test"  # Draft clone (typed FeaturePython)
  AttacherType = Attacher::AttachEngine3D
  Fuse = false
  Objects = -> [Part004]
  PathResource = Model
  Placement = pos=(15.5,-15.5,-0.9) rot=(0,0,1;0rad)
  Scale = (1,1,1)
FEATURE [App::DocumentObjectGroup] Model
  Group = -> [Clone]
FEATURE [TechDraw::DrawViewPart] View  label="FV"
  CoarseView = false
  Direction = (0,-1,0)
  Focus = 100
  HardHidden = true
  IsoCount = 0
  IsoHidden = false
  IsoVisible = false
  LockPosition = false
  Perspective = false
  Rotation = 0
  Scale = 2
  ScaleType = 0
  ScrubCount = 0
  SeamHidden = false
  SeamVisible = false
  SmoothHidden = false
  SmoothVisible = true
  Source = -> [Part004]
  X = 68.572
  XDirection = (1,0,0)
  Y = 132.596
FEATURE [TechDraw::DrawViewDimension] Dimension
  AngleOverride = false
  Arbitrary = false
  ArbitraryTolerances = false
  EqualTolerance = true
  ExtensionAngle = 0
  FormatSpec = %.2w
  FormatSpecOverTolerance = %+.2w
  FormatSpecUnderTolerance = %+.2w
  Inverted = false
  LineAngle = 0
  LockPosition = false
  MeasureType = 1
  OverTolerance = 0
  References2D = -> [View]
  Rotation = 0
  Scale = 2
  ScaleType = 0
  TheoreticalExact = false
  Type = 2
  UnderTolerance = 0
  X = 58.4117
  Y = 1.7767
FEATURE [TechDraw::DrawViewPart] View001  label="TV"
  CoarseView = false
  Direction = (0,0,1)
  Focus = 100
  HardHidden = false
  IsoCount = 0
  IsoHidden = false
  IsoVisible = false
  LockPosition = false
  Perspective = false
  Rotation = 0
  Scale = 2
  ScaleType = 0
  ScrubCount = 0
  SeamHidden = false
  SeamVisible = false
  SmoothHidden = false
  SmoothVisible = true
  Source = -> [Part004]
  X = 207.518
  XDirection = (1,0,0)
  Y = 128.995
FEATURE [TechDraw::DrawViewDimension] Dimension005
  AngleOverride = false
  Arbitrary = false
  ArbitraryTolerances = false
  EqualTolerance = true
  ExtensionAngle = 0
  FormatSpec = ⌀%.2w
  FormatSpecOverTolerance = %+.2w
  FormatSpecUnderTolerance = %+.2w
  Inverted = false
  LineAngle = 0
  LockPosition = false
  MeasureType = 1
  OverTolerance = 0
  References2D = -> [View001]
  Rotation = 0
  Scale = 2
  ScaleType = 0
  TheoreticalExact = false
  Type = 5
  UnderTolerance = 0
  X = -35.9434
  Y = 19.7776
FEATURE [TechDraw::DrawViewDimension] Dimension006
  AngleOverride = false
  Arbitrary = false
  ArbitraryTolerances = false
  EqualTolerance = true
  ExtensionAngle = 0
  FormatSpec = ⌀%.2w
  FormatSpecOverTolerance = %+.2w
  FormatSpecUnderTolerance = %+.2w
  Inverted = false
  LineAngle = 0
  LockPosition = false
  MeasureType = 1
  OverTolerance = 0
  References2D = -> [View001]
  Rotation = 0
  Scale = 2
  ScaleType = 0
  TheoreticalExact = false
  Type = 5
  UnderTolerance = 0
  X = -38.3086
  Y = 45.9214
FEATURE [TechDraw::DrawViewDimension] Dimension007
  AngleOverride = false
  Arbitrary = false
  ArbitraryTolerances = false
  EqualTolerance = true
  ExtensionAngle = 0
  FormatSpec = R%.2w
  FormatSpecOverTolerance = %+.2w
  FormatSpecUnderTolerance = %+.2w
  Inverted = false
  LineAngle = 0
  LockPosition = false
  MeasureType = 1
  OverTolerance = 0
  References2D = -> [View001]
  Rotation = 0
  Scale = 2
  ScaleType = 0
  TheoreticalExact = false
  Type = 4
  UnderTolerance = 0
  X = 27.5133
  Y = -6.14658
FEATURE [TechDraw::DrawViewDimension] Dimension008
  AngleOverride = false
  Arbitrary = false
  ArbitraryTolerances = false
  EqualTolerance = true
  ExtensionAngle = 0
  FormatSpec = R%.2w
  FormatSpecOverTolerance = %+.2w
  FormatSpecUnderTolerance = %+.2w
  Inverted = false
  LineAngle = 0
  LockPosition = false
  MeasureType = 1
  OverTolerance = 0
  References2D = -> [View001]
  Rotation = 0
  Scale = 2
  ScaleType = 0
  TheoreticalExact = false
  Type = 4
  UnderTolerance = 0
  X = 19.7569
  Y = -17.708
FEATURE [TechDraw::DrawViewDimension] Dimension009
  AngleOverride = false
  Arbitrary = false
  ArbitraryTolerances = false
  EqualTolerance = true
  ExtensionAngle = 0
  FormatSpec = %.2w
  FormatSpecOverTolerance = %+.2w
  FormatSpecUnderTolerance = %+.2w
  Inverted = false
  LineAngle = 0
  LockPosition = false
  MeasureType = 1
  OverTolerance = 0
  References2D = -> [View001]
  Rotation = 0
  Scale = 2
  ScaleType = 0
  TheoreticalExact = false
  Type = 0
  UnderTolerance = 0
  X = -30.6923
  Y = -19.3505
FEATURE [TechDraw::DrawViewDimension] Dimension010
  AngleOverride = false
  Arbitrary = false
  ArbitraryTolerances = false
  EqualTolerance = true
  ExtensionAngle = 0
  FormatSpec = %.2w
  FormatSpecOverTolerance = %+.2w
  FormatSpecUnderTolerance = %+.2w
  Inverted = false
  LineAngle = 0
  LockPosition = false
  MeasureType = 1
  OverTolerance = 0
  References2D = -> [View001]
  Rotation = 0
  Scale = 2
  ScaleType = 0
  TheoreticalExact = false
  Type = 1
  UnderTolerance = 0
  X = -3.16806
  Y = 42.0985
FEATURE [TechDraw::DrawViewDimension] Dimension018
  AngleOverride = false
  Arbitrary = false
  ArbitraryTolerances = false
  EqualTolerance = true
  ExtensionAngle = 0
  FormatSpec = %.2w
  FormatSpecOverTolerance = %+.2w
  FormatSpecUnderTolerance = %+.2w
  Inverted = false
  LineAngle = 0
  LockPosition = false
  MeasureType = 1
  OverTolerance = 0
  References2D = -> [View]
  Rotation = 0
  Scale = 2
  ScaleType = 0
  TheoreticalExact = false
  Type = 2
  UnderTolerance = 0
  X = 34.3585
  Y = -16.9904
FEATURE [TechDraw::DrawViewDimension] Dimension019
  AngleOverride = false
  Arbitrary = false
  ArbitraryTolerances = false
  EqualTolerance = true
  ExtensionAngle = 0
  FormatSpec = %.2w
  FormatSpecOverTolerance = %+.2w
  FormatSpecUnderTolerance = %+.2w
  Inverted = false
  LineAngle = 0
  LockPosition = false
  MeasureType = 1
  OverTolerance = 0
  References2D = -> [View]
  Rotation = 0
  Scale = 2
  ScaleType = 0
  TheoreticalExact = false
  Type = 1
  UnderTolerance = 0
  X = -2.5505
  Y = -21.8466
FEATURE [App::DocumentObjectGroup] Group001  label="Parts"
  Group = -> [Part005,Part001,Part002]
FEATURE [TechDraw::DrawViewDimension] Dimension020
  AngleOverride = false
  Arbitrary = false
  ArbitraryTolerances = false
  EqualTolerance = true
  ExtensionAngle = 0
  FormatSpec = %.2w
  FormatSpecOverTolerance = %+.2w
  FormatSpecUnderTolerance = %+.2w
  Inverted = false
  LineAngle = 0
  LockPosition = false
  MeasureType = 1
  OverTolerance = 0
  References2D = -> [View]
  Rotation = 0
  Scale = 2
  ScaleType = 0
  TheoreticalExact = false
  Type = 2
  UnderTolerance = 0
  X = 43.7631
  Y = -18.3438
FEATURE [TechDraw::DrawViewDimension] Dimension021
  AngleOverride = false
  Arbitrary = false
  ArbitraryTolerances = false
  EqualTolerance = true
  ExtensionAngle = 0
  FormatSpec = %.2w
  FormatSpecOverTolerance = %+.2w
  FormatSpecUnderTolerance = %+.2w
  Inverted = false
  LineAngle = 0
  LockPosition = false
  MeasureType = 1
  OverTolerance = 0
  References2D = -> [View]
  Rotation = 0
  Scale = 2
  ScaleType = 0
  TheoreticalExact = false
  Type = 1
  UnderTolerance = 0
  X = -0.807016
  Y = -31.5017
FEATURE [TechDraw::DrawViewDimension] Dimension022
  AngleOverride = false
  Arbitrary = false
  ArbitraryTolerances = false
  EqualTolerance = true
  ExtensionAngle = 0
  FormatSpec = %.2w
  FormatSpecOverTolerance = %+.2w
  FormatSpecUnderTolerance = %+.2w
  Inverted = false
  LineAngle = 0
  LockPosition = false
  MeasureType = 1
  OverTolerance = 0
  References2D = -> [View]
  Rotation = 0
  Scale = 2
  ScaleType = 0
  TheoreticalExact = false
  Type = 2
  UnderTolerance = 0
  X = 28.1761
  Y = 21.875
FEATURE [TechDraw::DrawViewDimension] Dimension023
  AngleOverride = false
  Arbitrary = false
  ArbitraryTolerances = false
  EqualTolerance = true
  ExtensionAngle = 0
  FormatSpec = %.2w
  FormatSpecOverTolerance = %+.2w
  FormatSpecUnderTolerance = %+.2w
  Inverted = false
  LineAngle = 0
  LockPosition = false
  MeasureType = 1
  OverTolerance = 0
  References2D = -> [View]
  Rotation = 0
  Scale = 2
  ScaleType = 0
  TheoreticalExact = false
  Type = 1
  UnderTolerance = 0
  X = 0.197119
  Y = -40.9016
FEATURE [TechDraw::DrawPage] Page  label="Starlock Adapter Glue type"
  KeepUpdated = true
  NextBalloonIndex = 1
  ProjectionType = 0
  Scale = 2
  Template = -> Template
  Views = -> [View,Dimension,View001,Dimension005,Dimension006,Dimension007,Dimension008,Dimension009,Dimension010,Dimension018,Dimension019,Dimension020,Dimension021,Dimension022,Dimension023]
FEATURE [App::DocumentObjectGroup] Group  label="Drawings"
  Group = -> [Page001,Page]
FEATURE [Part::FeaturePython] Stock  # WARN: FeaturePython — macro-defined, semantics opaque (R4)
  Base = -> Model
  ExtXneg = 1
  ExtXpos = 1
  ExtYneg = 1
  ExtYpos = 1
  ExtZneg = 0
  ExtZpos = 0
  Placement = pos=(1,-30,-9.3) rot=(0,0,1;0rad)
  StockType = FromBase
FEATURE [Path::FeaturePython] Adaptive  label="Facing glue base using Adaptive clearing"  # Path/CAM operation (typed FeaturePython)
  Active = false
  Base = -> [Clone]
  ClearanceHeight = 5
  CoolantMode = 1
  CycleTime = 00:02:59
  ExtensionCorners = true
  ExtensionLengthDefault = 3
  FinalDepth = -0.1
  FinishDepth = 0
  FinishingProfile = true
  ForceInsideOut = false
  HelixAngle = 1
  HelixConeAngle = 0
  HelixDiameterLimit = 0
  KeepToolDownRatio = 3
  LiftDistance = 0
  OpFinalDepth = -0.9
  OpStartDepth = 0
  OpStockZMax = 0
  OpStockZMin = -9.3
  OpToolDiameter = 6
  OperationType = 0
  SafeHeight = 0.5
  Side = 1
  StartDepth = 0
  StepDown = 0.45
  StepOver = 30
  StockToLeave = 0
  StopProcessing = false
  Stopped = false
  Tolerance = 0.1
  ToolController = -> __mmEndMill
  UseHelixArcs = false
  UseOutline = false
  expr: ClearanceHeight = OpStockZMax + SetupSheet.ClearanceHeightOffset
  expr: ExtensionLengthDefault = OpToolDiameter / 2
  expr: FinalDepth = -Spreadsheet.FacingDepth
  expr: SafeHeight = OpStockZMax + SetupSheet.SafeHeightOffset
  expr: StartDepth = 0
  expr: StepDown = Spreadsheet.StepDown
  expr: StepOver = 30
FEATURE [Path::FeaturePython] Adaptive001  label="Facing using Adaptive clearing"  # Path/CAM operation (typed FeaturePython)
  Active = false
  Base = -> [Clone]
  ClearanceHeight = 5
  CoolantMode = 1
  CycleTime = 00:03:42
  ExtensionCorners = true
  ExtensionLengthDefault = 1.5
  FinalDepth = -0.1
  FinishDepth = 0
  FinishingProfile = true
  ForceInsideOut = true
  HelixAngle = 5
  HelixConeAngle = 0
  HelixDiameterLimit = 0
  KeepToolDownRatio = 3
  LiftDistance = 0
  OpFinalDepth = -0.9
  OpStartDepth = 0
  OpStockZMax = 0
  OpStockZMin = -9.3
  OpToolDiameter = 3
  OperationType = 0
  SafeHeight = 0.5
  Side = 1
  StartDepth = 0
  StepDown = 0.45
  StepOver = 60
  StockToLeave = 0
  StopProcessing = false
  Stopped = false
  Tolerance = 0.1
  ToolController = -> __mmEndMill
  UseHelixArcs = false
  UseOutline = false
  expr: ClearanceHeight = OpStockZMax + SetupSheet.ClearanceHeightOffset
  expr: ExtensionLengthDefault = OpToolDiameter / 2
  expr: FinalDepth = -Spreadsheet.FacingDepth
  expr: SafeHeight = OpStockZMax + SetupSheet.SafeHeightOffset
  expr: StartDepth = 0
  expr: StepDown = Spreadsheet.StepDown
  expr: StepOver = 60
FEATURE [Path::FeaturePython] Profile009  label="CleaningupEdge"  # Path/CAM operation (typed FeaturePython)
  Active = false
  AreaParams:
    Tolerance = 1e-07
    FitArcs = True
    Simplify = False
    CleanDistance = 0.0
    Accuracy = 0.01
    Unit = 1.0
    MinArcPoints = 4
    MaxArcPoints = 100
    ClipperScale = 10000000.0
    Fill = 0
    Coplanar = 0
    Reorient = True
    Outline = False
    Explode = False
    OpenMode = 0
    Deflection = 0.01
    SubjectFill = 0
    ClipFill = 0
    Offset = 0.5
    ExtraPass = 0
    Stepover = 0.0
    LastStepover = 0.0
    JoinType = 0
    EndType = 0
    MiterLimit = 2.0
    RoundPrecision = 0.0
    PocketMode = 0
    ToolRadius = 1.0
    PocketExtraOffset = 0.0
    PocketStepover = 0.0
    PocketLastStepover = 0.0
    FromCenter = False
    Angle = 45.0
    AngleShift = 0.0
    Shift = 0.0
    Thicken = False
    SectionCount = -1
    Stepdown = 1.0
    SectionOffset = 0.0
    SectionTolerance = 1e-06
    SectionMode = 2
    Project = False
  Base = -> [Clone]
  ClearanceHeight = 5
  CoolantMode = 1
  CycleTime = 00:01:13
  Direction = 0
  FinalDepth = -0.1
  HandleMultipleFeatures = 0
  JoinType = 0
  MiterLimit = 0.1
  OffsetExtra = -1
  OpFinalDepth = -0.9
  OpStartDepth = 0
  OpStockZMax = 0
  OpStockZMin = -9.3
  OpToolDiameter = 3
  PathParams = {'orientation': 1, 'feedrate': 3.0, 'feedrate_v': 0.3333333333333333, 'verbose': True, 'resume_height': 0.5, 'retraction': 5.0, 'return_end': True, 'preamble': False}
  SafeHeight = 0.5
  Side = 0
  SplitArcs = false
  StartDepth = 0
  StartPoint = (0,0,0)
  StepDown = 0.45
  ToolController = -> __mmEndMill
  UseComp = true
  UseStartPoint = false
  processCircles = false
  processHoles = false
  processPerimeter = true
  expr: ClearanceHeight = OpStockZMax + SetupSheet.ClearanceHeightOffset
  expr: FinalDepth = -Spreadsheet.FacingDepth
  expr: SafeHeight = OpStockZMax + SetupSheet.SafeHeightOffset
  expr: StartDepth = 0
  expr: StepDown = Spreadsheet.StepDown
FEATURE [Path::FeaturePython] LeadInOutDressup  label="CleaningupFacedEdge"  # Path/CAM operation (typed FeaturePython)
  Base = -> Profile009
  ExtendLeadIn = 0
  ExtendLeadOut = 0
  IncludeLayers = true
  KeepToolDown = false
  LeadIn = true
  LeadOut = true
  Length = 2.25
  LengthOut = 2.25
  RapidPlunge = true
  StyleOff = 0
  StyleOn = 0
FEATURE [Path::FeaturePython] Profile010  label="MillEdge"  # Path/CAM operation (typed FeaturePython)
  Active = false
  AreaParams:
    Tolerance = 1e-07
    FitArcs = True
    Simplify = False
    CleanDistance = 0.0
    Accuracy = 0.01
    Unit = 1.0
    MinArcPoints = 4
    MaxArcPoints = 100
    ClipperScale = 10000000.0
    Fill = 0
    Coplanar = 0
    Reorient = True
    Outline = False
    Explode = False
    OpenMode = 0
    Deflection = 0.01
    SubjectFill = 0
    ClipFill = 0
    Offset = -1.0
    ExtraPass = 0
    Stepover = 0.0
    LastStepover = 0.0
    JoinType = 0
    EndType = 0
    MiterLimit = 2.0
    RoundPrecision = 0.0
    PocketMode = 0
    ToolRadius = 1.0
    PocketExtraOffset = 0.0
    PocketStepover = 0.0
    PocketLastStepover = 0.0
    FromCenter = False
    Angle = 45.0
    AngleShift = 0.0
    Shift = 0.0
    Thicken = False
    SectionCount = -1
    Stepdown = 1.0
    SectionOffset = 0.0
    SectionTolerance = 1e-06
    SectionMode = 2
    Project = False
  Base = -> [Clone]
  ClearanceHeight = 5
  CoolantMode = 1
  CycleTime = 00:01:49
  Direction = 0
  FinalDepth = -1
  HandleMultipleFeatures = 0
  JoinType = 0
  MiterLimit = 0.1
  OffsetExtra = -2.5
  OpFinalDepth = -0.9
  OpStartDepth = 0
  OpStockZMax = 0
  OpStockZMin = -9.3
  OpToolDiameter = 3
  PathParams = {'orientation': 1, 'feedrate': 3.0, 'feedrate_v': 0.3333333333333333, 'verbose': True, 'resume_height': 0.5, 'retraction': 5.0, 'return_end': True, 'preamble': False}
  SafeHeight = 0.5
  Side = 0
  SplitArcs = false
  StartDepth = 0
  StartPoint = (0,0,0)
  StepDown = 0.45
  ToolController = -> __mmEndMill
  UseComp = true
  UseStartPoint = false
  processCircles = false
  processHoles = false
  processPerimeter = true
  expr: ClearanceHeight = OpStockZMax + SetupSheet.ClearanceHeightOffset
  expr: FinalDepth = -Spreadsheet.CuttingDepth
  expr: SafeHeight = OpStockZMax + SetupSheet.SafeHeightOffset
  expr: StartDepth = 0
  expr: StepDown = Spreadsheet.StepDown
FEATURE [Path::FeaturePython] Profile011  label="MillProfileRough"  # Path/CAM operation (typed FeaturePython)
  Active = false
  AreaParams:
    Tolerance = 1e-07
    FitArcs = True
    Simplify = False
    CleanDistance = 0.0
    Accuracy = 0.01
    Unit = 1.0
    MinArcPoints = 4
    MaxArcPoints = 100
    ClipperScale = 10000000.0
    Fill = 0
    Coplanar = 0
    Reorient = True
    Outline = False
    Explode = False
    OpenMode = 0
    Deflection = 0.01
    SubjectFill = 0
    ClipFill = 0
    Offset = 4.2
    ExtraPass = 0
    Stepover = 0.0
    LastStepover = 0.0
    JoinType = 0
    EndType = 0
    MiterLimit = 2.0
    RoundPrecision = 0.0
    PocketMode = 0
    ToolRadius = 1.0
    PocketExtraOffset = 0.0
    PocketStepover = 0.0
    PocketLastStepover = 0.0
    FromCenter = False
    Angle = 45.0
    AngleShift = 0.0
    Shift = 0.0
    Thicken = False
    SectionCount = -1
    Stepdown = 1.0
    SectionOffset = 0.0
    SectionTolerance = 1e-06
    SectionMode = 2
    Project = False
  Base = -> [Clone]
  ClearanceHeight = 5
  CoolantMode = 1
  CycleTime = 00:01:43
  Direction = 0
  FinalDepth = -1
  HandleMultipleFeatures = 0
  JoinType = 0
  MiterLimit = 0.1
  OffsetExtra = 2.7
  OpFinalDepth = -2.2e-15
  OpStartDepth = 0.45
  OpStockZMax = 0
  OpStockZMin = -9.3
  OpToolDiameter = 3
  PathParams = {'orientation': 1, 'feedrate': 3.0, 'feedrate_v': 0.3333333333333333, 'verbose': True, 'resume_height': 0.5, 'retraction': 5.0, 'return_end': True, 'preamble': False}
  SafeHeight = 0.5
  Side = 0
  SplitArcs = false
  StartDepth = 0
  StartPoint = (0,0,0)
  StepDown = 0.45
  ToolController = -> __mmEndMill
  UseComp = true
  UseStartPoint = false
  processCircles = false
  processHoles = false
  processPerimeter = true
  expr: ClearanceHeight = OpStockZMax + SetupSheet.ClearanceHeightOffset
  expr: FinalDepth = -Spreadsheet.CuttingDepth
  expr: OffsetExtra = Spreadsheet.ExtraOffsetRoughing
  expr: SafeHeight = OpStockZMax + SetupSheet.SafeHeightOffset
  expr: StartDepth = 0
  expr: StepDown = Spreadsheet.StepDown
FEATURE [Path::FeaturePython] Profile012  label="MillProfile"  # Path/CAM operation (typed FeaturePython)
  Active = false
  AreaParams:
    Tolerance = 1e-07
    FitArcs = True
    Simplify = False
    CleanDistance = 0.0
    Accuracy = 0.01
    Unit = 1.0
    MinArcPoints = 4
    MaxArcPoints = 100
    ClipperScale = 10000000.0
    Fill = 0
    Coplanar = 0
    Reorient = True
    Outline = False
    Explode = False
    OpenMode = 0
    Deflection = 0.01
    SubjectFill = 0
    ClipFill = 0
    Offset = 1.7
    ExtraPass = 0
    Stepover = 0.0
    LastStepover = 0.0
    JoinType = 0
    EndType = 0
    MiterLimit = 2.0
    RoundPrecision = 0.0
    PocketMode = 0
    ToolRadius = 1.0
    PocketExtraOffset = 0.0
    PocketStepover = 0.0
    PocketLastStepover = 0.0
    FromCenter = False
    Angle = 45.0
    AngleShift = 0.0
    Shift = 0.0
    Thicken = False
    SectionCount = -1
    Stepdown = 1.0
    SectionOffset = 0.0
    SectionTolerance = 1e-06
    SectionMode = 2
    Project = False
  Base = -> [Clone]
  ClearanceHeight = 5
  CoolantMode = 1
  CycleTime = 00:01:42
  Direction = 0
  FinalDepth = -1
  HandleMultipleFeatures = 0
  JoinType = 0
  MiterLimit = 0.1
  OffsetExtra = 0.2
  OpFinalDepth = -2.2e-15
  OpStartDepth = 0.45
  OpStockZMax = 0
  OpStockZMin = -9.3
  OpToolDiameter = 3
  PathParams = {'orientation': 1, 'feedrate': 3.0, 'feedrate_v': 0.3333333333333333, 'verbose': True, 'resume_height': 0.5, 'retraction': 5.0, 'return_end': True, 'preamble': False}
  SafeHeight = 0.5
  Side = 0
  SplitArcs = false
  StartDepth = 0
  StartPoint = (0,0,0)
  StepDown = 0.45
  ToolController = -> __mmEndMill
  UseComp = true
  UseStartPoint = false
  processCircles = false
  processHoles = false
  processPerimeter = true
  expr: ClearanceHeight = OpStockZMax + SetupSheet.ClearanceHeightOffset
  expr: FinalDepth = -Spreadsheet.CuttingDepth
  expr: OffsetExtra = Spreadsheet.StockToLeaveProfilePass
  expr: SafeHeight = OpStockZMax + SetupSheet.SafeHeightOffset
  expr: StartDepth = 0
  expr: StepDown = Spreadsheet.StepDown
FEATURE [Path::FeaturePython] LeadInOutDressup001  label="MillEdge"  # Path/CAM operation (typed FeaturePython)
  Base = -> Profile010
  ExtendLeadIn = 0
  ExtendLeadOut = 0
  IncludeLayers = true
  KeepToolDown = false
  LeadIn = true
  LeadOut = true
  Length = 2.25
  LengthOut = 2.25
  RapidPlunge = true
  StyleOff = 0
  StyleOn = 0
FEATURE [Path::FeaturePython] LeadInOutDressup002  label="MillProfileRough"  # Path/CAM operation (typed FeaturePython)
  Base = -> Profile011
  ExtendLeadIn = 0
  ExtendLeadOut = 0
  IncludeLayers = true
  KeepToolDown = false
  LeadIn = true
  LeadOut = true
  Length = 2.25
  LengthOut = 2.25
  RapidPlunge = true
  StyleOff = 0
  StyleOn = 0
FEATURE [Path::FeaturePython] LeadInOutDressup003  label="MillProfile"  # Path/CAM operation (typed FeaturePython)
  Base = -> Profile012
  ExtendLeadIn = 0
  ExtendLeadOut = 0
  IncludeLayers = true
  KeepToolDown = false
  LeadIn = true
  LeadOut = true
  Length = 2.25
  LengthOut = 2.25
  RapidPlunge = true
  StyleOff = 0
  StyleOn = 0
FEATURE [Path::FeaturePython] Profile013  label="MillProfileFinish"  # Path/CAM operation (typed FeaturePython)
  Active = true
  AreaParams:
    Tolerance = 1e-07
    FitArcs = True
    Simplify = False
    CleanDistance = 0.0
    Accuracy = 0.01
    Unit = 1.0
    MinArcPoints = 4
    MaxArcPoints = 100
    ClipperScale = 10000000.0
    Fill = 0
    Coplanar = 0
    Reorient = True
    Outline = False
    Explode = False
    OpenMode = 0
    Deflection = 0.01
    SubjectFill = 0
    ClipFill = 0
    Offset = 1.45
    ExtraPass = 0
    Stepover = 0.0
    LastStepover = 0.0
    JoinType = 0
    EndType = 0
    MiterLimit = 2.0
    RoundPrecision = 0.0
    PocketMode = 0
    ToolRadius = 1.0
    PocketExtraOffset = 0.0
    PocketStepover = 0.0
    PocketLastStepover = 0.0
    FromCenter = False
    Angle = 45.0
    AngleShift = 0.0
    Shift = 0.0
    Thicken = False
    SectionCount = -1
    Stepdown = 1.0
    SectionOffset = 0.0
    SectionTolerance = 1e-06
    SectionMode = 2
    Project = False
  Base = -> [Clone]
  ClearanceHeight = 5
  CoolantMode = 1
  CycleTime = 00:01:22
  Direction = 0
  FinalDepth = -1
  HandleMultipleFeatures = 0
  JoinType = 0
  MiterLimit = 0.1
  OffsetExtra = -0.05
  OpFinalDepth = -2.2e-15
  OpStartDepth = 1
  OpStockZMax = 0
  OpStockZMin = -9.3
  OpToolDiameter = 3
  PathParams = {'orientation': 1, 'feedrate': 2.0, 'feedrate_v': 0.3333333333333333, 'verbose': True, 'resume_height': 0.5, 'retraction': 5.0, 'return_end': True, 'preamble': False}
  SafeHeight = 0.5
  Side = 0
  SplitArcs = false
  StartDepth = 0
  StartPoint = (0,0,0)
  StepDown = 1
  ToolController = -> __mmEndMill001
  UseComp = true
  UseStartPoint = false
  processCircles = false
  processHoles = false
  processPerimeter = true
  expr: ClearanceHeight = OpStockZMax + SetupSheet.ClearanceHeightOffset
  expr: FinalDepth = -Spreadsheet.CuttingDepth
  expr: OffsetExtra = Spreadsheet.StockToLeaveFinishPass
  expr: SafeHeight = OpStockZMax + SetupSheet.SafeHeightOffset
  expr: StartDepth = 0
  expr: StepDown = Spreadsheet.CuttingDepth
FEATURE [Path::FeaturePython] LeadInOutDressup004  label="MillProfileFinish"  # Path/CAM operation (typed FeaturePython)
  Base = -> Profile013
  ExtendLeadIn = 0
  ExtendLeadOut = 0
  IncludeLayers = true
  KeepToolDown = false
  LeadIn = true
  LeadOut = true
  Length = 2.25
  LengthOut = 2.25
  RapidPlunge = true
  StyleOff = 0
  StyleOn = 0
FEATURE [Path::FeaturePython] Profile014  label="MillProfileCleanupFaceTop"  # Path/CAM operation (typed FeaturePython)
  Active = true
  AreaParams:
    Tolerance = 1e-07
    FitArcs = True
    Simplify = False
    CleanDistance = 0.0
    Accuracy = 0.01
    Unit = 1.0
    MinArcPoints = 4
    MaxArcPoints = 100
    ClipperScale = 10000000.0
    Fill = 0
    Coplanar = 0
    Reorient = True
    Outline = False
    Explode = False
    OpenMode = 0
    Deflection = 0.01
    SubjectFill = 0
    ClipFill = 0
    Offset = 1.0
    ExtraPass = 0
    Stepover = 0.0
    LastStepover = 0.0
    JoinType = 0
    EndType = 0
    MiterLimit = 2.0
    RoundPrecision = 0.0
    PocketMode = 0
    ToolRadius = 1.0
    PocketExtraOffset = 0.0
    PocketStepover = 0.0
    PocketLastStepover = 0.0
    FromCenter = False
    Angle = 45.0
    AngleShift = 0.0
    Shift = 0.0
    Thicken = False
    SectionCount = -1
    Stepdown = 1.0
    SectionOffset = 0.0
    SectionTolerance = 1e-06
    SectionMode = 2
    Project = False
  Base = -> [Clone]
  ClearanceHeight = 5
  CoolantMode = 1
  CycleTime = 00:01:06
  Direction = 0
  FinalDepth = -0.1
  HandleMultipleFeatures = 0
  JoinType = 0
  MiterLimit = 0.1
  OffsetExtra = -0.5
  OpFinalDepth = -2.2e-15
  OpStartDepth = 1
  OpStockZMax = 0
  OpStockZMin = -9.3
  OpToolDiameter = 3
  PathParams = {'orientation': 1, 'feedrate': 3.0, 'feedrate_v': 0.3333333333333333, 'verbose': True, 'resume_height': 0.5, 'retraction': 5.0, 'return_end': True, 'preamble': False}
  SafeHeight = 0.5
  Side = 0
  SplitArcs = false
  StartDepth = 0
  StartPoint = (0,0,0)
  StepDown = 1
  ToolController = -> __mmEndMill
  UseComp = true
  UseStartPoint = false
  processCircles = false
  processHoles = false
  processPerimeter = true
  expr: ClearanceHeight = OpStockZMax + SetupSheet.ClearanceHeightOffset
  expr: FinalDepth = -Spreadsheet.FacingDepth
  expr: SafeHeight = OpStockZMax + SetupSheet.SafeHeightOffset
  expr: StartDepth = 0
  expr: StepDown = Spreadsheet.CuttingDepth
FEATURE [Path::FeaturePython] LeadInOutDressup005  label="MillProfileCleanupFaceTop"  # Path/CAM operation (typed FeaturePython)
  Base = -> Profile014
  ExtendLeadIn = 0
  ExtendLeadOut = 0
  IncludeLayers = true
  KeepToolDown = false
  LeadIn = true
  LeadOut = true
  Length = 2.25
  LengthOut = 2.25
  RapidPlunge = true
  StyleOff = 0
  StyleOn = 0
FEATURE [App::DocumentObjectGroup] Operations
  Group = -> [Adaptive,Adaptive001,LeadInOutDressup,LeadInOutDressup001,LeadInOutDressup002,LeadInOutDressup003,LeadInOutDressup004,LeadInOutDressup005]
FEATURE [Path::FeaturePython] Job  label="Starlock Adapter Glue type"  # Path/CAM operation (typed FeaturePython)
  CycleTime = 00:02:28
  Fixtures = G54
  GeometryTolerance = 0.01
  JobType = 0
  LastPostProcessDate = 2024-02-11 19:26:26.326376
  LastPostProcessOutput = <path>
  Model = -> Model
  Operations = -> Operations
  OrderOutputBy = 0
  PostProcessor = 11
  PostProcessorOutputFile = //tablethp/c<userpath>/Desktop/CNC programs/StarLink.nc
  SetupSheet = -> SetupSheet
  SplitOutput = false
  Stock = -> Stock
  Tools = -> Tools
note: 5 file-system paths scrubbed to <path> (originals preserved in the JSON sidecar)
